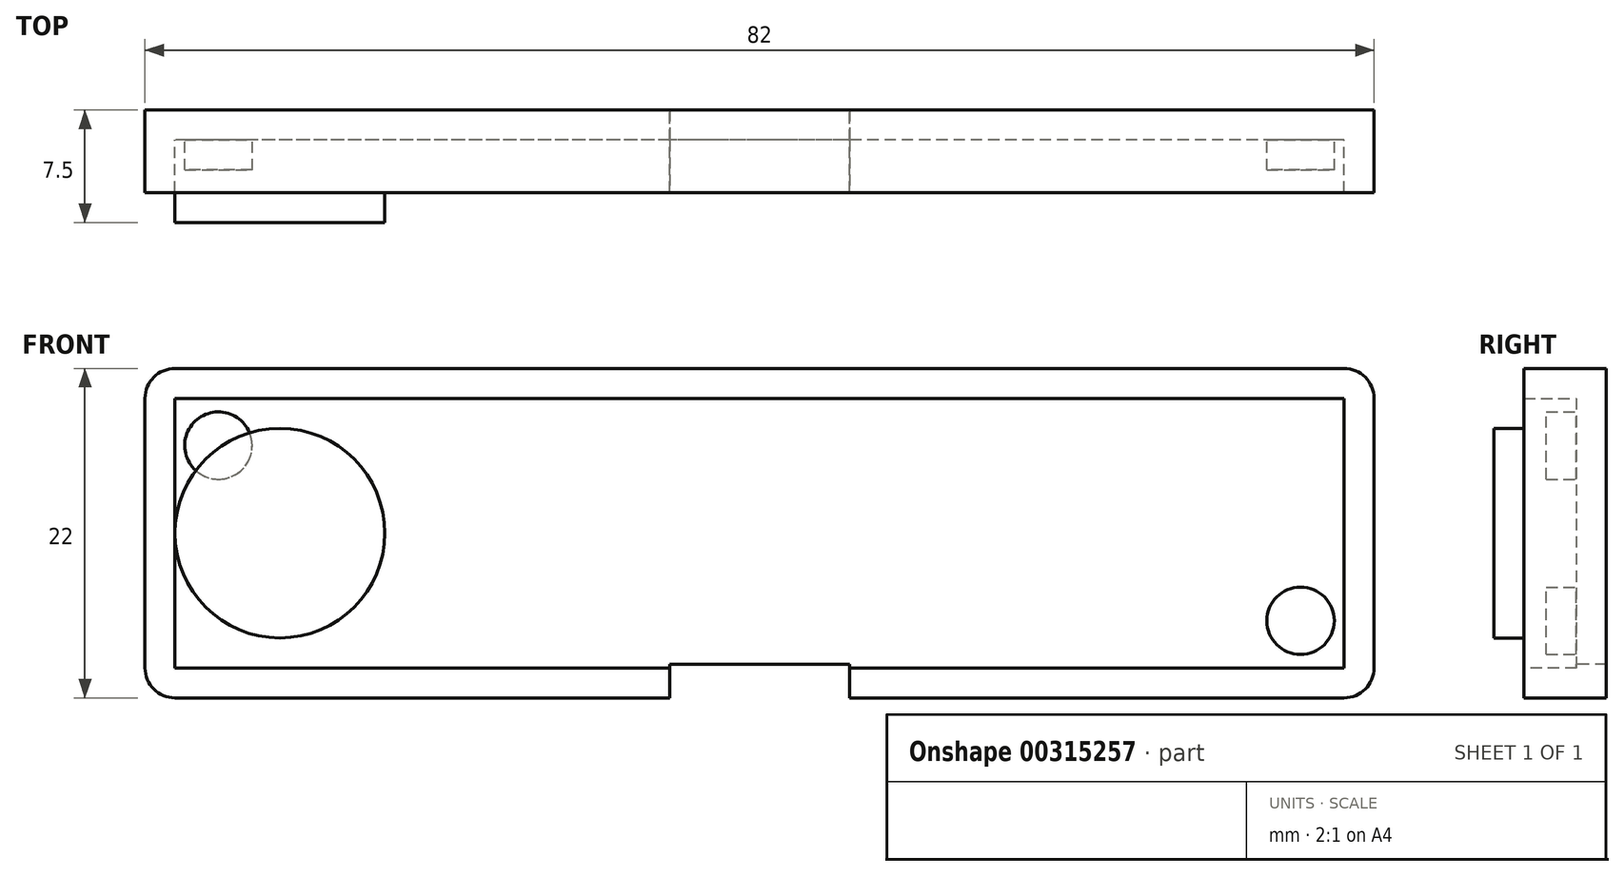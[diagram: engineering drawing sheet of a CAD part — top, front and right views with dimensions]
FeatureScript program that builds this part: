
annotation { "Feature Type Name" : "Feature", "Feature Type Description" : "" }
export const myFeature = defineFeature(function(context is Context, id is Id, definition is map)
    precondition{}
    {
        {
            var Q0;
            Q0=qCreatedBy(makeId("Front.planeOp"),FACE);
            var sketch = newSketch(context, id + "F0", { "sketchPlane" : qUnion([Q0])});
            skLineSegment(sketch, "E0.bottom", {"start": v(41, 11) * mm, "end": v(-41, 11) * mm});
            skLineSegment(sketch, "E0.top", {"start": v(41, -11) * mm, "end": v(-41, -11) * mm});
            skLineSegment(sketch, "E0.left", {"start": v(41, 11) * mm, "end": v(41, -11) * mm});
            skLineSegment(sketch, "E0.right", {"start": v(-41, 11) * mm, "end": v(-41, -11) * mm});
            skPoint(sketch, "E0.middle", {"position": v(0, 0) * mm});
            skSolve(sketch);
        }
        {
            var Q0;
            Q0=qCreatedBy(makeId("Front.planeOp"),FACE);
            var sketch = newSketch(context, id + "F1", { "sketchPlane" : qUnion([Q0])});
            skCircle(sketch, "E1", {"center": v(-36.1, 5.85) * mm, "radius": 2.25 * mm});
            skCircle(sketch, "E2", {"center": v(36.1, -5.85) * mm, "radius": 2.25 * mm});
            skSolve(sketch);
        }
        {
            var Q0;
            Q0 = qSketchRegion(id + "F0", true);
            extrude(context, id + "F2", {"entities" : qUnion([Q0]), "oppositeDirection" : true, "depth" : 2 * mm, "offsetDistance" : 25 * mm});
        }
        {
            var Q0;
            Q0 = qSketchRegion(id + "F1", true);
            extrude(context, id + "F3", {"entities" : qUnion([Q0]), "operationType" : NewBodyOperationType.ADD, "depth" : 2 * mm});
        }
        {
            var Q0;
            Q0=makeQuery(id+"F2.opExtrude","CAP_FACE",FACE,{"disambiguationData":[OSD([sQuery(id+"F0.wireOp",EDGE,"E0.bottom"),sQuery(id+"F0.wireOp",EDGE,"E0.top"),sQuery(id+"F0.wireOp",EDGE,"E0.left"),sQuery(id+"F0.wireOp",EDGE,"E0.right")])],"isStart":true});
            var sketch = newSketch(context, id + "F4", { "sketchPlane" : qUnion([Q0])});
            skLineSegment(sketch, "E3.bottom", {"start": v(39, 9) * mm, "end": v(-39, 9) * mm});
            skLineSegment(sketch, "E3.top", {"start": v(39, -9) * mm, "end": v(-39, -9) * mm});
            skLineSegment(sketch, "E3.left", {"start": v(39, 9) * mm, "end": v(39, -9) * mm});
            skLineSegment(sketch, "E3.right", {"start": v(-39, 9) * mm, "end": v(-39, -9) * mm});
            skPoint(sketch, "E3.middle", {"position": v(0, 0) * mm});
            skSolve(sketch);
        }
        {
            var Q0;
            Q0=makeQuery(id+"F4.imprint","IMPRINT",FACE,{"disambiguationData":[TD([[makeQuery(id+"F4.imprint","IMPRINT",EDGE,{"derivedFrom":sQuery(id+"F4.wireOp",EDGE,"E3.bottom")}),-1.0]])]});
            extrude(context, id + "F5", {"entities" : qUnion([Q0]), "operationType" : NewBodyOperationType.ADD, "depth" : 3.5 * mm});
        }
        {
            var Q0;
            Q0=makeQuery(id+"F5.opExtrude","CAP_FACE",FACE,{"disambiguationData":[OSD([sQuery(id+"F0.wireOp",EDGE,"E0.bottom"),sQuery(id+"F0.wireOp",EDGE,"E0.top"),sQuery(id+"F0.wireOp",EDGE,"E0.left"),sQuery(id+"F0.wireOp",EDGE,"E0.right"),sQuery(id+"F4.wireOp",EDGE,"E3.bottom"),sQuery(id+"F4.wireOp",EDGE,"E3.top"),sQuery(id+"F4.wireOp",EDGE,"E3.left"),sQuery(id+"F4.wireOp",EDGE,"E3.right")])],"isStart":false});
            var sketch = newSketch(context, id + "F6", { "sketchPlane" : qUnion([Q0])});
            skLineSegment(sketch, "E4.bottom", {"start": v(6, -11.25) * mm, "end": v(-6, -11.25) * mm});
            skLineSegment(sketch, "E4.top", {"start": v(6, -8.75) * mm, "end": v(-6, -8.75) * mm});
            skLineSegment(sketch, "E4.left", {"start": v(6, -11.25) * mm, "end": v(6, -8.75) * mm});
            skLineSegment(sketch, "E4.right", {"start": v(-6, -11.25) * mm, "end": v(-6, -8.75) * mm});
            skPoint(sketch, "E4.middle", {"position": v(0, -10) * mm});
            skPoint(sketch, "E5", {"position": v(0, -9) * mm});
            skLineSegment(sketch, "E6", {"start": v(-10, -10) * mm, "end": v(10, -10) * mm, "construction": true});
            skSolve(sketch);
        }
        {
            var Q0;
            Q0 = qSketchRegion(id + "F6", true);
            var Q1;
            Q1=makeQuery(id+"F2.opExtrude","CAP_FACE",FACE,{"disambiguationData":[OSD([sQuery(id+"F0.wireOp",EDGE,"E0.bottom"),sQuery(id+"F0.wireOp",EDGE,"E0.top"),sQuery(id+"F0.wireOp",EDGE,"E0.left"),sQuery(id+"F0.wireOp",EDGE,"E0.right")])],"isStart":false});
            extrude(context, id + "F7", {"entities" : qUnion([Q0]), "operationType" : NewBodyOperationType.REMOVE, "endBound" : BoundingType.UP_TO_SURFACE, "oppositeDirection" : true, "endBoundEntityFace" : qUnion([Q1]), "depth" : 5 * mm});
        }
        {
            var Q0;
            {var subQ0=sQuery(id+"F0.wireOp",EDGE,"E0.right");var subQ1=sQuery(id+"F0.wireOp",EDGE,"E0.bottom");Q0=makeQuery(id+"F5.boolean.opBoolean","MERGE",EDGE,{"derivedFrom":[makeQuery(id+"F2.opExtrude","SWEPT_EDGE",EDGE,{"disambiguationData":[OSD([subQ1,subQ0])]}),makeQuery(id+"F5.opExtrude","SWEPT_EDGE",EDGE,{"disambiguationData":[OSD([subQ1,subQ0])]})]});}
            var Q1;
            {var subQ0=sQuery(id+"F0.wireOp",EDGE,"E0.left");var subQ1=sQuery(id+"F0.wireOp",EDGE,"E0.bottom");Q1=makeQuery(id+"F5.boolean.opBoolean","MERGE",EDGE,{"derivedFrom":[makeQuery(id+"F2.opExtrude","SWEPT_EDGE",EDGE,{"disambiguationData":[OSD([subQ1,subQ0])]}),makeQuery(id+"F5.opExtrude","SWEPT_EDGE",EDGE,{"disambiguationData":[OSD([subQ1,subQ0])]})]});}
            var Q2;
            {var subQ0=sQuery(id+"F0.wireOp",EDGE,"E0.left");var subQ1=sQuery(id+"F0.wireOp",EDGE,"E0.top");Q2=makeQuery(id+"F5.boolean.opBoolean","MERGE",EDGE,{"derivedFrom":[makeQuery(id+"F2.opExtrude","SWEPT_EDGE",EDGE,{"disambiguationData":[OSD([subQ1,subQ0])]}),makeQuery(id+"F5.opExtrude","SWEPT_EDGE",EDGE,{"disambiguationData":[OSD([subQ1,subQ0])]})]});}
            var Q3;
            {var subQ0=sQuery(id+"F0.wireOp",EDGE,"E0.right");var subQ1=sQuery(id+"F0.wireOp",EDGE,"E0.top");Q3=makeQuery(id+"F5.boolean.opBoolean","MERGE",EDGE,{"derivedFrom":[makeQuery(id+"F2.opExtrude","SWEPT_EDGE",EDGE,{"disambiguationData":[OSD([subQ1,subQ0])]}),makeQuery(id+"F5.opExtrude","SWEPT_EDGE",EDGE,{"disambiguationData":[OSD([subQ1,subQ0])]})]});}
            fillet(context, id + "F8", {"entities" : qUnion([Q0, Q1, Q2, Q3]), "radius" : 2 * mm, "tangentPropagation" : true, "allowEdgeOverflow" : false});
        }
        {
            var Q0;
            Q0=makeQuery(id+"F6.imprint","IMPRINT",FACE,{"disambiguationData":[TD([[makeQuery(id+"F6.imprint","IMPRINT",EDGE,{"derivedFrom":makeQuery(id+"F5.opExtrude","CAP_EDGE",EDGE,{"disambiguationData":[OSD([sQuery(id+"F4.wireOp",EDGE,"E3.bottom")])],"isStart":false})}),-1.0]])]});
            var sketch = newSketch(context, id + "F9", { "sketchPlane" : qUnion([Q0])});
            skLineSegment(sketch, "E7.bottom", {"start": v(-41, 11) * mm, "end": v(41, 11) * mm});
            skLineSegment(sketch, "E7.top", {"start": v(-41, -11) * mm, "end": v(41, -11) * mm});
            skLineSegment(sketch, "E7.left", {"start": v(-41, 11) * mm, "end": v(-41, -11) * mm});
            skLineSegment(sketch, "E7.right", {"start": v(41, 11) * mm, "end": v(41, -11) * mm});
            skSolve(sketch);
        }
        {
            var Q0;
            Q0 = qSketchRegion(id + "F9", true);
            extrude(context, id + "F10", {"entities" : qUnion([Q0]), "depth" : 2 * mm, "offsetDistance" : 25 * mm});
        }
        {
            var Q0;
            Q0=makeQuery(id+"F10.opExtrude","SWEPT_EDGE",EDGE,{"disambiguationData":[OSD([sQuery(id+"F9.wireOp",EDGE,"E7.bottom"),sQuery(id+"F9.wireOp",EDGE,"E7.right")])]});
            var Q1;
            Q1=makeQuery(id+"F10.opExtrude","SWEPT_EDGE",EDGE,{"disambiguationData":[OSD([sQuery(id+"F9.wireOp",EDGE,"E7.top"),sQuery(id+"F9.wireOp",EDGE,"E7.right")])]});
            var Q2;
            Q2=makeQuery(id+"F10.opExtrude","SWEPT_EDGE",EDGE,{"disambiguationData":[OSD([sQuery(id+"F9.wireOp",EDGE,"E7.top"),sQuery(id+"F9.wireOp",EDGE,"E7.left")])]});
            var Q3;
            Q3=makeQuery(id+"F10.opExtrude","SWEPT_EDGE",EDGE,{"disambiguationData":[OSD([sQuery(id+"F9.wireOp",EDGE,"E7.bottom"),sQuery(id+"F9.wireOp",EDGE,"E7.left")])]});
            fillet(context, id + "F11", {"entities" : qUnion([Q0, Q1, Q2, Q3]), "radius" : 2 * mm, "tangentPropagation" : true, "allowEdgeOverflow" : false});
        }
        {
            var Q0;
            Q0=makeQuery(id+"F10.opExtrude","CAP_FACE",FACE,{"disambiguationData":[OSD([sQuery(id+"F9.wireOp",EDGE,"E7.bottom"),sQuery(id+"F9.wireOp",EDGE,"E7.top"),sQuery(id+"F9.wireOp",EDGE,"E7.left"),sQuery(id+"F9.wireOp",EDGE,"E7.right")])],"isStart":false});
            var sketch = newSketch(context, id + "F12", { "sketchPlane" : qUnion([Q0])});
            skCircle(sketch, "E8", {"center": v(32, 0) * mm, "radius": 7 * mm});
            skPoint(sketch, "E8.centerSnap0", {"position": v(41, 0) * mm});
            skCircle(sketch, "E9.MirrorC", {"center": v(-32, 0) * mm, "radius": 7 * mm});
            skSolve(sketch);
        }
        {
            var Q0;
            Q0=makeQuery(id+"F12.imprint","IMPRINT",FACE,{"disambiguationData":[TD([[makeQuery(id+"F12.imprint","IMPRINT",EDGE,{"derivedFrom":sQuery(id+"F12.wireOp",EDGE,"E9.MirrorC")}),-1.0]])]});
            var Q1;
            Q1=makeQuery(id+"F12.imprint","IMPRINT",FACE,{"disambiguationData":[TD([[makeQuery(id+"F12.imprint","IMPRINT",EDGE,{"derivedFrom":sQuery(id+"F12.wireOp",EDGE,"E8")}),1.0]])]});
            extrude(context, id + "F13", {"entities" : qUnion([Q0, Q1]), "operationType" : NewBodyOperationType.REMOVE, "oppositeDirection" : true, "depth" : 2 * mm, "offsetDistance" : 25 * mm});
        }
    });
